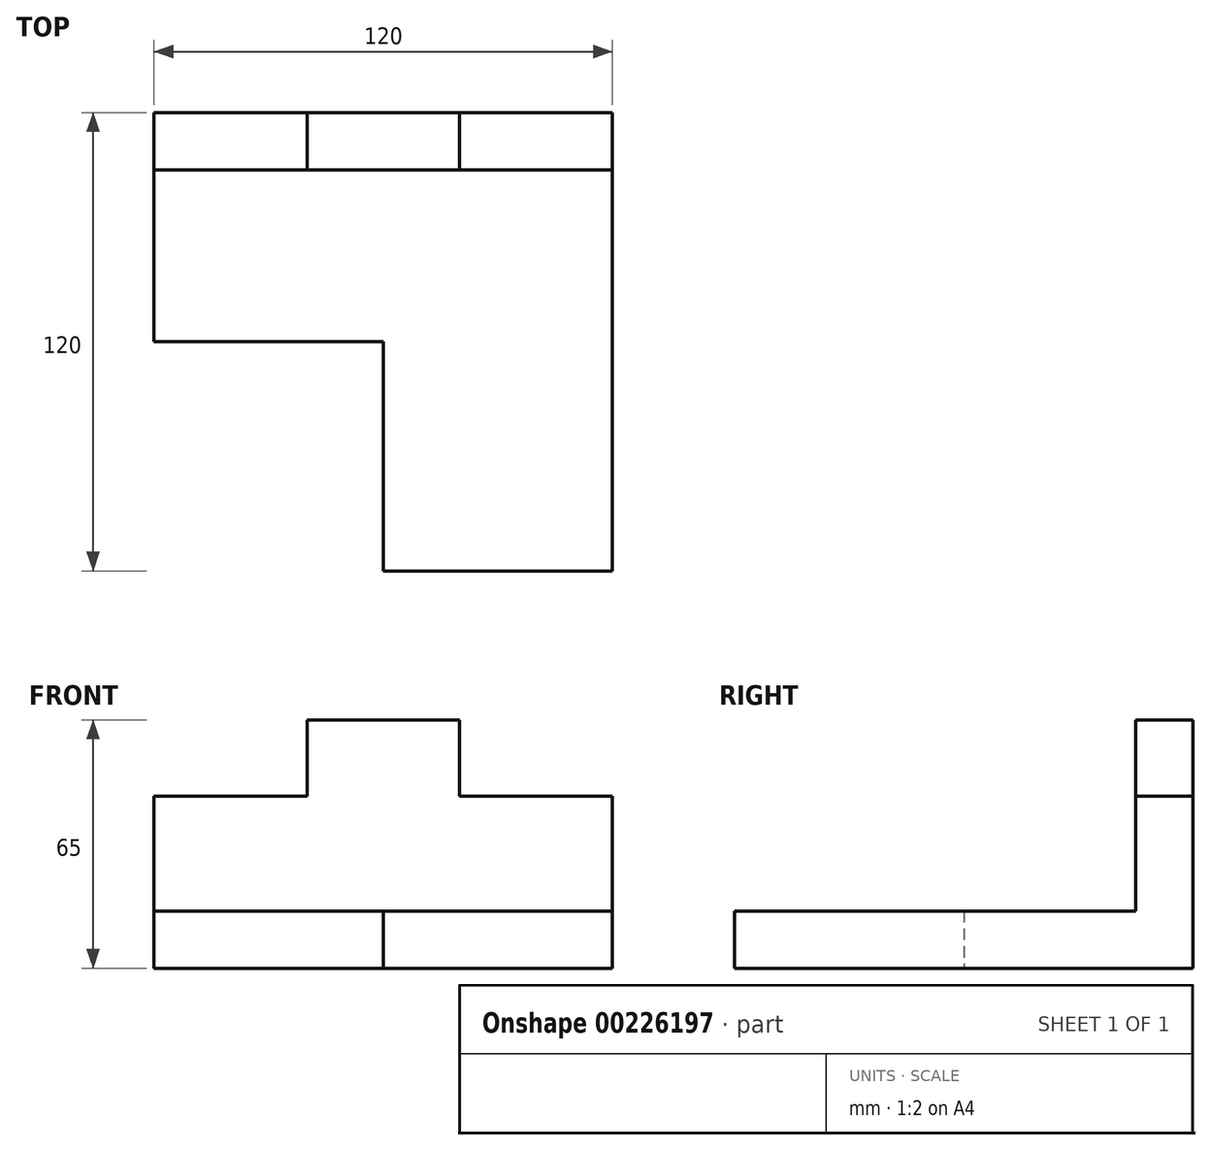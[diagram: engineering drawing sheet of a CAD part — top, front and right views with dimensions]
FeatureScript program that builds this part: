
annotation { "Feature Type Name" : "Feature", "Feature Type Description" : "" }
export const myFeature = defineFeature(function(context is Context, id is Id, definition is map)
    precondition{}
    {
        {
            var Q0;
            Q0=qCreatedBy(makeId("Top.planeOp"),FACE);
            var sketch = newSketch(context, id + "F0", { "sketchPlane" : qUnion([Q0])});
            skLineSegment(sketch, "E0.bottom", {"start": v(0, 0) * mm, "end": v(-120, 0) * mm});
            skLineSegment(sketch, "E0.top", {"start": v(0, -120) * mm, "end": v(-120, -120) * mm});
            skLineSegment(sketch, "E0.left", {"start": v(0, 0) * mm, "end": v(0, -120) * mm});
            skLineSegment(sketch, "E0.right", {"start": v(-120, 0) * mm, "end": v(-120, -120) * mm});
            skLineSegment(sketch, "E1.bottom", {"start": v(-120, -120) * mm, "end": v(-60, -120) * mm});
            skLineSegment(sketch, "E1.top", {"start": v(-120, -60) * mm, "end": v(-60, -60) * mm});
            skLineSegment(sketch, "E1.left", {"start": v(-120, -120) * mm, "end": v(-120, -60) * mm});
            skLineSegment(sketch, "E1.right", {"start": v(-60, -120) * mm, "end": v(-60, -60) * mm});
            skSolve(sketch);
        }
        {
            var Q0;
            Q0=makeQuery(id+"F0.imprint","IMPRINT",FACE,{"disambiguationData":[TD([[makeQuery(id+"F0.imprint","IMPRINT",EDGE,{"derivedFrom":sQuery(id+"F0.wireOp",EDGE,"E0.bottom")}),1.0]])]});
            extrude(context, id + "F1", {"entities" : qUnion([Q0]), "depth" : 15 * mm});
        }
        {
            var Q0;
            Q0=qCreatedBy(makeId("Front.planeOp"),FACE);
            var sketch = newSketch(context, id + "F2", { "sketchPlane" : qUnion([Q0])});
            skLineSegment(sketch, "E2.bottom", {"start": v(0, 0) * mm, "end": v(-120, 0) * mm});
            skLineSegment(sketch, "E2.top", {"start": v(0, 65) * mm, "end": v(-120, 65) * mm});
            skLineSegment(sketch, "E2.left", {"start": v(0, 0) * mm, "end": v(0, 65) * mm});
            skLineSegment(sketch, "E2.right", {"start": v(-120, 0) * mm, "end": v(-120, 65) * mm});
            skLineSegment(sketch, "E3.bottom", {"start": v(0, 65) * mm, "end": v(-40, 65) * mm});
            skLineSegment(sketch, "E3.top", {"start": v(0, 45) * mm, "end": v(-40, 45) * mm});
            skLineSegment(sketch, "E3.left", {"start": v(0, 65) * mm, "end": v(0, 45) * mm});
            skLineSegment(sketch, "E3.right", {"start": v(-40, 65) * mm, "end": v(-40, 45) * mm});
            skLineSegment(sketch, "E4", {"start": v(-60, 65) * mm, "end": v(-60, 0) * mm, "construction": true});
            skLineSegment(sketch, "E5.MirrorCS", {"start": v(-120, 45) * mm, "end": v(-80, 45) * mm});
            skLineSegment(sketch, "E6.MirrorCS", {"start": v(-80, 65) * mm, "end": v(-80, 45) * mm});
            skSolve(sketch);
        }
        {
            var Q0;
            {var subQ1=sQuery(id+"F2.wireOp",EDGE,"E2.bottom");Q0=makeQuery(id+"F2.imprint","IMPRINT",FACE,{"disambiguationData":[TD([[makeQuery(id+"F2.imprint","IMPRINT",EDGE,{"derivedFrom":subQ1}),-1.0]])]});}
            extrude(context, id + "F3", {"entities" : qUnion([Q0]), "operationType" : NewBodyOperationType.ADD, "depth" : 15 * mm});
        }
    });
